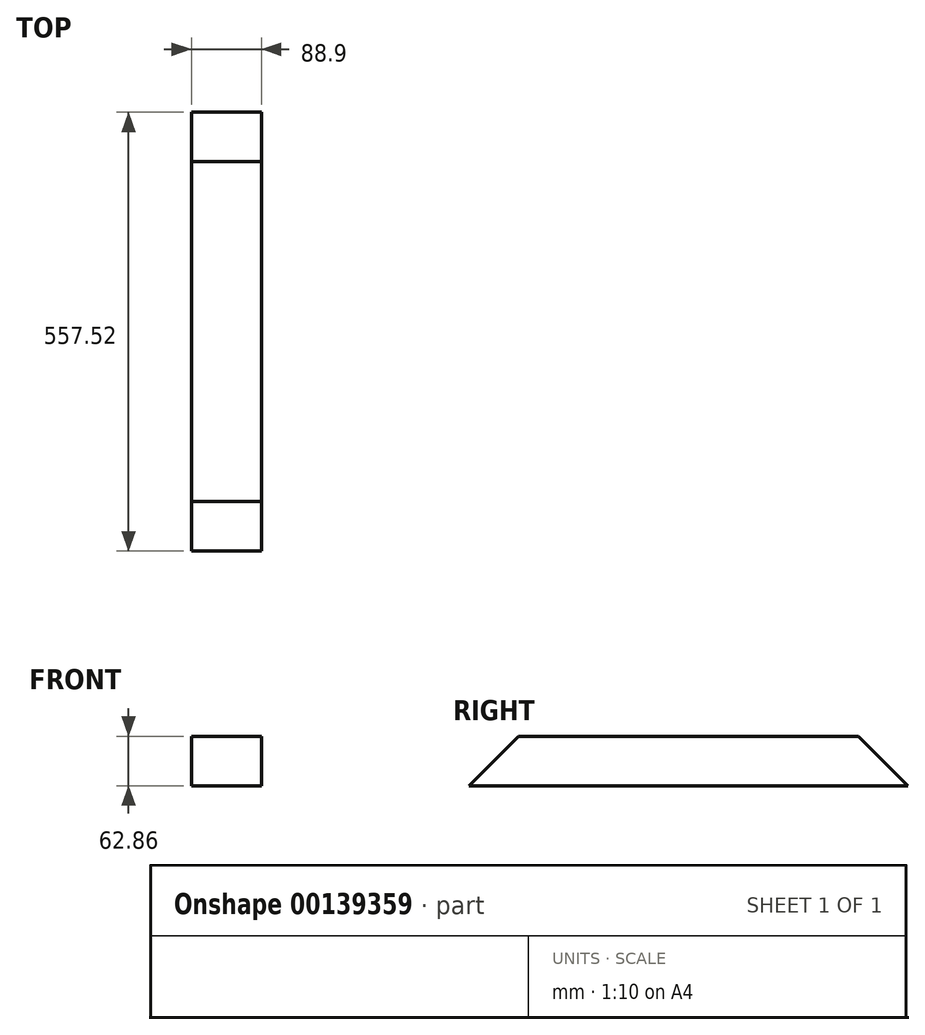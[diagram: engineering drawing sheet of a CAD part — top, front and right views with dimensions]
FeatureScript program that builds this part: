
annotation { "Feature Type Name" : "Feature", "Feature Type Description" : "" }
export const myFeature = defineFeature(function(context is Context, id is Id, definition is map)
    precondition{}
    {
        {
            var Q0;
            Q0=qCreatedBy(makeId("Right.planeOp"),FACE);
            var sketch = newSketch(context, id + "F0", { "sketchPlane" : qUnion([Q0])});
            skLineSegment(sketch, "E0", {"start": v(-390.53, 62.86) * mm, "end": v(-453.4, 0) * mm});
            skLineSegment(sketch, "E1", {"start": v(-453.4, 0) * mm, "end": v(-453.4, 0) * mm});
            skLineSegment(sketch, "E2", {"start": v(41.27, 62.86) * mm, "end": v(-390.53, 62.86) * mm});
            skLineSegment(sketch, "E3", {"start": v(104.13, 0) * mm, "end": v(41.27, 62.86) * mm});
            skLineSegment(sketch, "E4", {"start": v(-453.4, 0) * mm, "end": v(104.13, 0) * mm});
            skSolve(sketch);
        }
        {
            var Q0;
            Q0=makeQuery(id+"F0.imprint","IMPRINT",FACE,{"disambiguationData":[TD([[makeQuery(id+"F0.imprint","IMPRINT",EDGE,{"derivedFrom":sQuery(id+"F0.wireOp",EDGE,"E0")}),1.0]])]});
            extrude(context, id + "F1", {"entities" : qUnion([Q0]), "depth" : 88.9 * mm});
        }
    });
